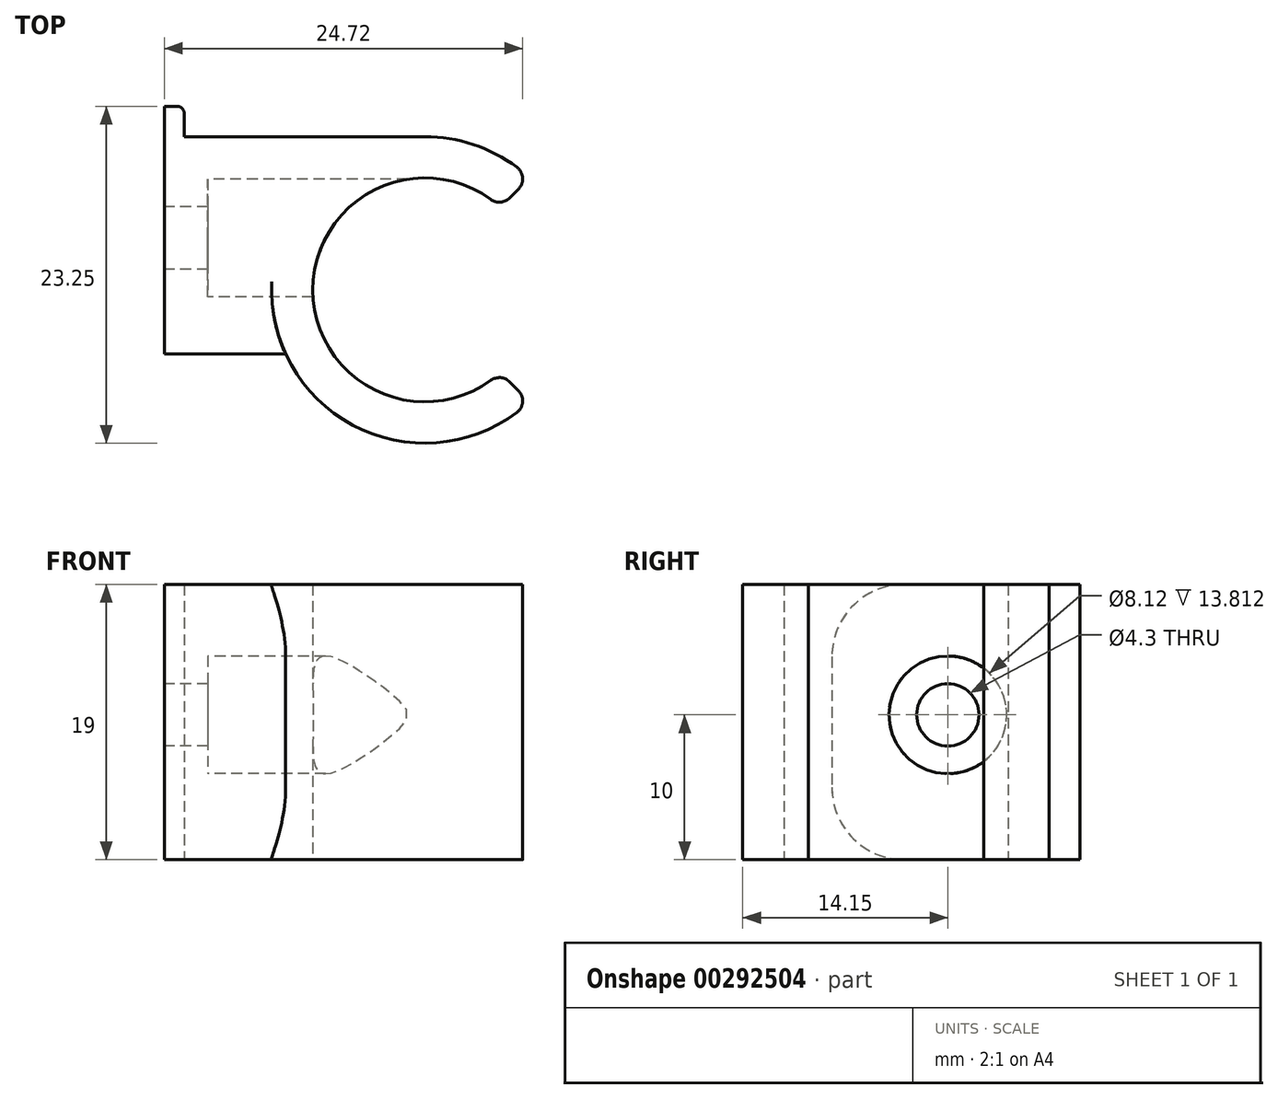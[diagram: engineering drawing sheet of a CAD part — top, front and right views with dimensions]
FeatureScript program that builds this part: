
annotation { "Feature Type Name" : "Feature", "Feature Type Description" : "" }
export const myFeature = defineFeature(function(context is Context, id is Id, definition is map)
    precondition{}
    {
        {
            var Q0;
            Q0=qCreatedBy(makeId("Top.planeOp"),FACE);
            var sketch = newSketch(context, id + "F0", { "sketchPlane" : qUnion([Q0])});
            skArc(sketch, "E0", {"start": v(-27.83, 12.89) * mm, "mid": v(-44.75, 4.42) * mm, "end": v(-27.83, -4.03) * mm});
            skArc(sketch, "E1", {"start": v(-29.63, 10.67) * mm, "mid": v(-41.9, 4.42) * mm, "end": v(-29.63, -1.82) * mm});
            skLineSegment(sketch, "E2.bottom", {"start": v(-34.18, 15) * mm, "end": v(-52.15, 15) * mm});
            skLineSegment(sketch, "E2.top", {"start": v(-40.5, 0) * mm, "end": v(-52.15, 0) * mm});
            skLineSegment(sketch, "E2.left", {"start": v(-34.18, 15) * mm, "end": v(-34.18, 12.15) * mm});
            skLineSegment(sketch, "E2.right", {"start": v(-52.15, 15) * mm, "end": v(-52.15, 0) * mm});
            skLineSegment(sketch, "E3.bottom", {"start": v(-52.15, 0) * mm, "end": v(-50.77, 0) * mm});
            skLineSegment(sketch, "E3.top", {"start": v(-52.15, 17.1) * mm, "end": v(-51.27, 17.1) * mm});
            skLineSegment(sketch, "E3.left", {"start": v(-52.15, 0) * mm, "end": v(-52.15, 17.1) * mm});
            skLineSegment(sketch, "E3.right", {"start": v(-50.77, 0) * mm, "end": v(-50.77, 16.6) * mm});
            skLineSegment(sketch, "E4", {"start": v(-28.33, -1.92) * mm, "end": v(-27.72, -2.53) * mm});
            skLineSegment(sketch, "E5", {"start": v(-28.33, 10.77) * mm, "end": v(-27.72, 11.38) * mm});
            skPoint(sketch, "E6.visualSharp", {"position": v(-26.95, 12.15) * mm});
            skArc(sketch, "E6.filletArc", {"start": v(-27.72, 11.38) * mm, "mid": v(-27.43, 12.16) * mm, "end": v(-27.83, 12.89) * mm});
            skPoint(sketch, "E7.visualSharp", {"position": v(-28.97, 10.13) * mm});
            skArc(sketch, "E7.filletArc", {"start": v(-29.63, 10.67) * mm, "mid": v(-28.96, 10.48) * mm, "end": v(-28.33, 10.77) * mm});
            skPoint(sketch, "E8.visualSharp", {"position": v(-28.97, -1.28) * mm});
            skArc(sketch, "E8.filletArc", {"start": v(-28.33, -1.92) * mm, "mid": v(-28.96, -1.63) * mm, "end": v(-29.63, -1.82) * mm});
            skPoint(sketch, "E9.visualSharp", {"position": v(-26.95, -3.3) * mm});
            skArc(sketch, "E9.filletArc", {"start": v(-27.83, -4.03) * mm, "mid": v(-27.43, -3.3) * mm, "end": v(-27.72, -2.53) * mm});
            skPoint(sketch, "E10.visualSharp", {"position": v(-50.77, 17.1) * mm});
            skArc(sketch, "E10.filletArc", {"start": v(-50.77, 16.6) * mm, "mid": v(-50.92, 16.95) * mm, "end": v(-51.27, 17.1) * mm});
            skSolve(sketch);
        }
        {
            var Q0;
            Q0 = qSketchRegion(id + "F0", true);
            extrude(context, id + "F1", {"entities" : qUnion([Q0]), "depth" : 19 * mm});
        }
        {
            var Q0;
            Q0=makeQuery(id+"F1.opExtrude","CAP_EDGE",EDGE,{"disambiguationData":[OSD([sQuery(id+"F0.wireOp",EDGE,"E2.top"),sQuery(id+"F0.wireOp",EDGE,"E3.bottom")])],"isStart":false});
            var Q1;
            Q1=makeQuery(id+"F1.opExtrude","CAP_EDGE",EDGE,{"disambiguationData":[OSD([sQuery(id+"F0.wireOp",EDGE,"E2.top"),sQuery(id+"F0.wireOp",EDGE,"E3.bottom")])],"isStart":true});
            fillet(context, id + "F2", {"entities" : qUnion([Q0, Q1]), "radius" : 5 * mm, "tangentPropagation" : true, "allowEdgeOverflow" : false});
        }
        {
            var Q0;
            Q0=makeQuery(id+"F1.opExtrude","SWEPT_FACE",FACE,{"disambiguationData":[OSD([sQuery(id+"F0.wireOp",EDGE,"E3.left")])]});
            var sketch = newSketch(context, id + "F3", { "sketchPlane" : qUnion([Q0])});
            skCircle(sketch, "E11", {"center": v(-8, 10) * mm, "radius": 4.06 * mm});
            skSolve(sketch);
        }
        {
            var Q0;
            Q0=makeQuery(id+"F3.imprint","IMPRINT",FACE,{"disambiguationData":[TD([[makeQuery(id+"F3.imprint","IMPRINT",EDGE,{"derivedFrom":sQuery(id+"F3.wireOp",EDGE,"E11")}),1.0]])]});
            extrude(context, id + "F4", {"entities" : qUnion([Q0]), "operationType" : NewBodyOperationType.REMOVE, "oppositeDirection" : true, "depth" : 17 * mm});
        }
        {
            var Q0;
            Q0=makeQuery(id+"F1.opExtrude","SWEPT_FACE",FACE,{"disambiguationData":[OSD([sQuery(id+"F0.wireOp",EDGE,"E3.left")])]});
            var sketch = newSketch(context, id + "F5", { "sketchPlane" : qUnion([Q0])});
            skCircle(sketch, "E12", {"center": v(-8, 10) * mm, "radius": 4.15 * mm});
            skCircle(sketch, "E13", {"center": v(-8, 10) * mm, "radius": 2.15 * mm});
            skSolve(sketch);
        }
        {
            var Q0;
            Q0=makeQuery(id+"F5.imprint","IMPRINT",FACE,{"disambiguationData":[TD([[makeQuery(id+"F5.imprint","IMPRINT",EDGE,{"derivedFrom":sQuery(id+"F5.wireOp",EDGE,"E13")}),-1.0]])]});
            extrude(context, id + "F6", {"entities" : qUnion([Q0]), "operationType" : NewBodyOperationType.ADD, "oppositeDirection" : true, "depth" : 3 * mm});
        }
    });
